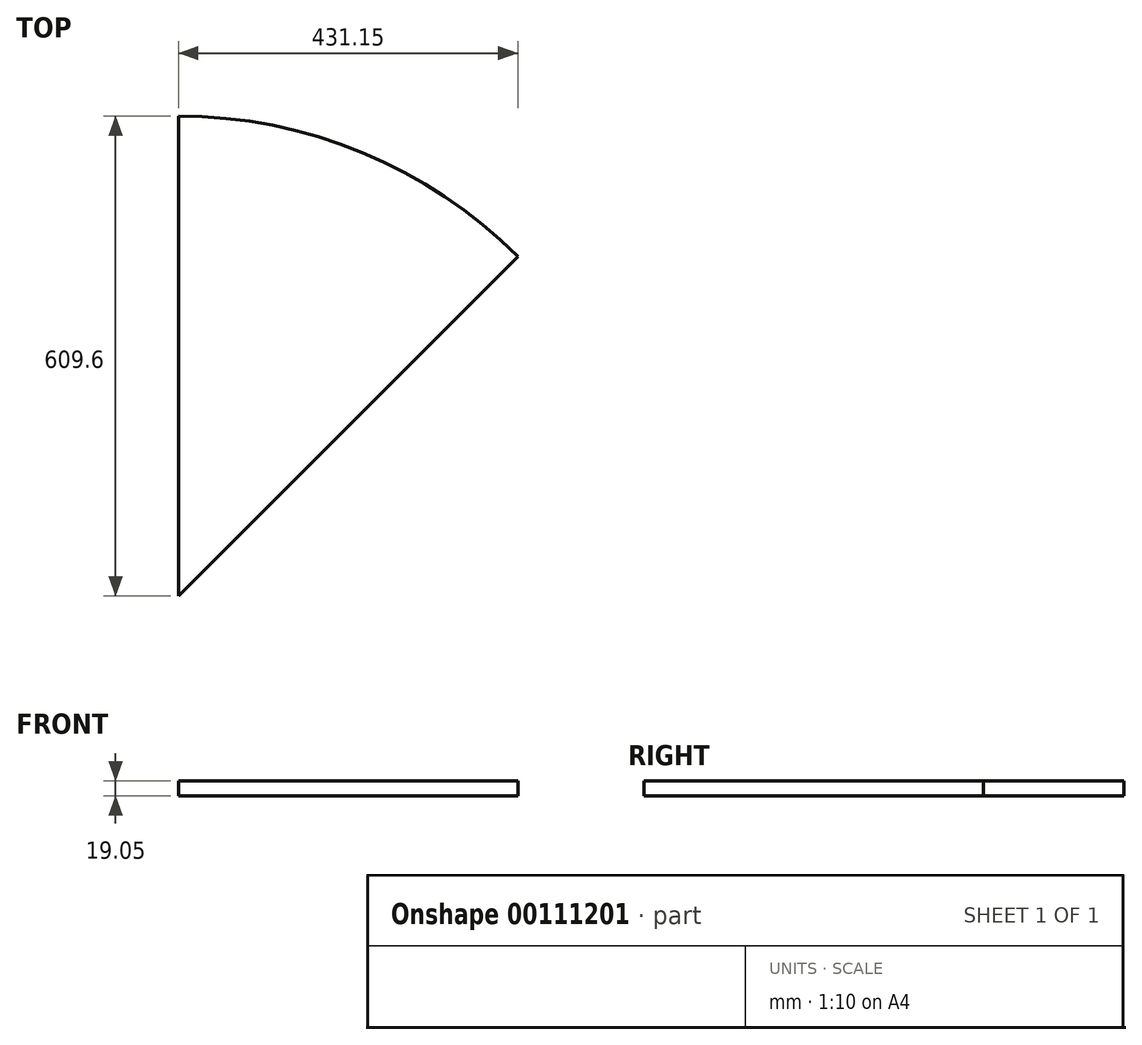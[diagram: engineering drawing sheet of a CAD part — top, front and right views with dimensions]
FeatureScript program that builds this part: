
annotation { "Feature Type Name" : "Feature", "Feature Type Description" : "" }
export const myFeature = defineFeature(function(context is Context, id is Id, definition is map)
    precondition{}
    {
        {
            var Q0;
            Q0=qCreatedBy(makeId("Top.planeOp"),FACE);
            var sketch = newSketch(context, id + "F0", { "sketchPlane" : qUnion([Q0])});
            skLineSegment(sketch, "E0", {"start": v(0, 0) * mm, "end": v(431.15, 431.15) * mm});
            skLineSegment(sketch, "E1", {"start": v(0, 609.6) * mm, "end": v(0, 0) * mm});
            skArc(sketch, "E2", {"start": v(431.15, 431.15) * mm, "mid": v(233.33, 563.26) * mm, "end": v(0, 609.6) * mm});
            skSolve(sketch);
        }
        {
            var Q0;
            Q0=makeQuery(id+"F0.imprint","IMPRINT",FACE,{"disambiguationData":[TD([[makeQuery(id+"F0.imprint","IMPRINT",EDGE,{"derivedFrom":sQuery(id+"F0.wireOp",EDGE,"E0")}),1.0]])]});
            extrude(context, id + "F1", {"entities" : qUnion([Q0]), "depth" : 19.05 * mm});
        }
    });
